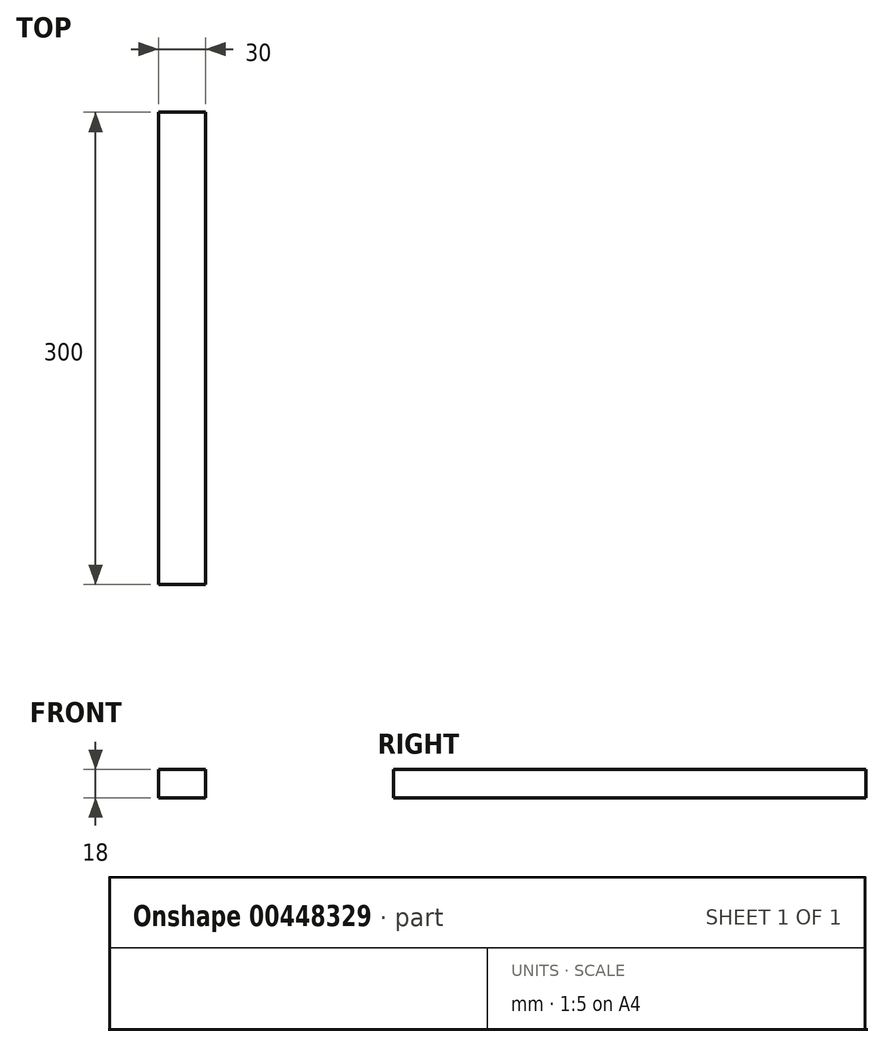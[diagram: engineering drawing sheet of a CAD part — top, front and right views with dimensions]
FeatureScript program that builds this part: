
annotation { "Feature Type Name" : "Feature", "Feature Type Description" : "" }
export const myFeature = defineFeature(function(context is Context, id is Id, definition is map)
    precondition{}
    {
        {
            var Q0;
            Q0=qCreatedBy(makeId("Top.planeOp"),FACE);
            var sketch = newSketch(context, id + "F0", { "sketchPlane" : qUnion([Q0])});
            skLineSegment(sketch, "E0.bottom", {"start": v(0, 0) * mm, "end": v(30, 0) * mm});
            skLineSegment(sketch, "E0.top", {"start": v(0, 300) * mm, "end": v(30, 300) * mm});
            skLineSegment(sketch, "E0.left", {"start": v(0, 0) * mm, "end": v(0, 300) * mm});
            skLineSegment(sketch, "E0.right", {"start": v(30, 0) * mm, "end": v(30, 300) * mm});
            skSolve(sketch);
        }
        {
            var Q0;
            Q0=makeQuery(id+"F0.imprint","IMPRINT",FACE,{"disambiguationData":[TD([[makeQuery(id+"F0.imprint","IMPRINT",EDGE,{"derivedFrom":sQuery(id+"F0.wireOp",EDGE,"E0.bottom")}),1.0]])]});
            extrude(context, id + "F1", {"entities" : qUnion([Q0]), "depth" : 18 * mm});
        }
    });
